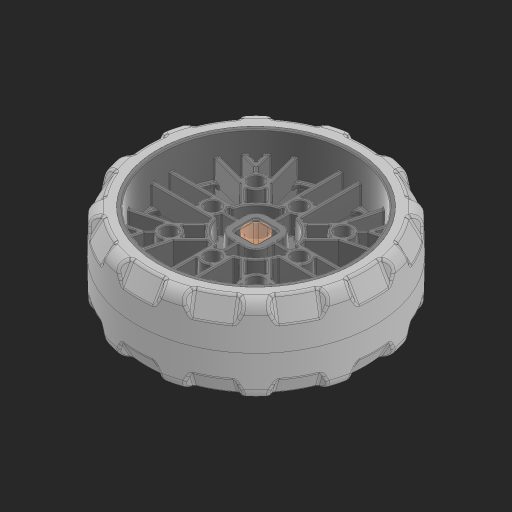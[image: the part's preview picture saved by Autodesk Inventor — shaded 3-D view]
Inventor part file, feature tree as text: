
AUTODESK INVENTOR PART (.ipt)
format: ipt  version: 2023 (Build 270158000, 158)  size: 6,804,992 bytes
history: native  units: in
note: dims shown in document units (in); Inventor stores cm internally (conversion verified against a paired STEP export)
features: other x3, sketch x1, extrude x1
ambient origin geometry x8: Origin, YZ Plane, XZ Plane, XY Plane, X Axis, Y Axis, Z Axis, Center Point
bodies: Solid1 (feature_tree), Solid2 (feature_tree)
feature tree (5):
  sketch  "Sketch1"  dims[d0=0.3937in d1=0.0in]
  other  "Srf1"
  other  "276-8098-001 Rev2_1:1"
  other  "276-8098-002 Rev2_2:1"
  extrude  "ExtrusionSrf1"  [1 undecoded]
note: 1 required parameter value undecoded (feature->parameter linkage not recoverable at this tier; creation-order binding heuristic only, values carry confidence <= 0.55)
